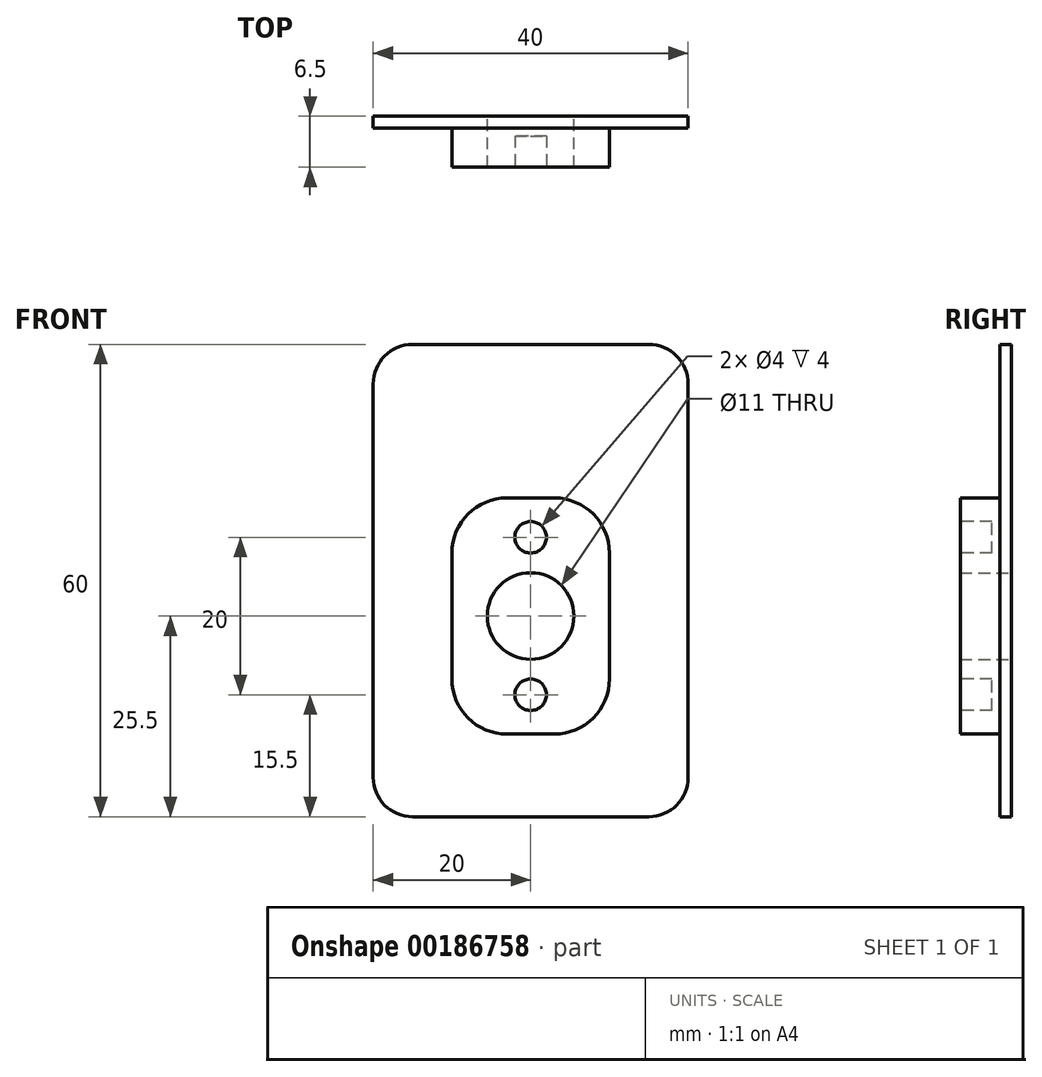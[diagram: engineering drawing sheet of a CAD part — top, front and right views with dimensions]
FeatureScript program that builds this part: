
annotation { "Feature Type Name" : "Feature", "Feature Type Description" : "" }
export const myFeature = defineFeature(function(context is Context, id is Id, definition is map)
    precondition{}
    {
        {
            var Q0;
            Q0=qCreatedBy(makeId("Front.planeOp"),FACE);
            var sketch = newSketch(context, id + "F0", { "sketchPlane" : qUnion([Q0])});
            skCircle(sketch, "E0", {"center": v(0, 0) * mm, "radius": 5.5 * mm});
            skLineSegment(sketch, "E1.bottom", {"start": v(20, -25.5) * mm, "end": v(-20, -25.5) * mm});
            skLineSegment(sketch, "E1.top", {"start": v(20, 34.5) * mm, "end": v(-20, 34.5) * mm});
            skLineSegment(sketch, "E1.left", {"start": v(20, -25.5) * mm, "end": v(20, 34.5) * mm});
            skLineSegment(sketch, "E1.right", {"start": v(-20, -25.5) * mm, "end": v(-20, 34.5) * mm});
            skSolve(sketch);
        }
        {
            var Q0;
            Q0=makeQuery(id+"F0.imprint","IMPRINT",FACE,{"disambiguationData":[TD([[makeQuery(id+"F0.imprint","IMPRINT",EDGE,{"derivedFrom":sQuery(id+"F0.wireOp",EDGE,"E0")}),-1.0]])]});
            extrude(context, id + "F1", {"entities" : qUnion([Q0]), "depth" : 1.5 * mm});
        }
        {
            var Q0;
            Q0=makeQuery(id+"F1.opExtrude","CAP_FACE",FACE,{"disambiguationData":[OSD([sQuery(id+"F0.wireOp",EDGE,"E0"),sQuery(id+"F0.wireOp",EDGE,"E1.bottom"),sQuery(id+"F0.wireOp",EDGE,"E1.top"),sQuery(id+"F0.wireOp",EDGE,"E1.left"),sQuery(id+"F0.wireOp",EDGE,"E1.right")])],"isStart":false});
            var sketch = newSketch(context, id + "F2", { "sketchPlane" : qUnion([Q0])});
            skLineSegment(sketch, "E2.bottom", {"start": v(-10, 15) * mm, "end": v(10, 15) * mm});
            skLineSegment(sketch, "E2.top", {"start": v(-10, -15) * mm, "end": v(10, -15) * mm});
            skLineSegment(sketch, "E2.left", {"start": v(-10, 15) * mm, "end": v(-10, -15) * mm});
            skLineSegment(sketch, "E2.right", {"start": v(10, 15) * mm, "end": v(10, -15) * mm});
            skPoint(sketch, "E2.middle", {"position": v(0, 0) * mm});
            skCircle(sketch, "E3", {"center": v(0, 0) * mm, "radius": 5.5 * mm});
            skSolve(sketch);
        }
        {
            var Q0;
            Q0 = qSketchRegion(id + "F2", true);
            extrude(context, id + "F3", {"entities" : qUnion([Q0]), "operationType" : NewBodyOperationType.ADD, "depth" : 5 * mm});
        }
        {
            var Q0;
            Q0=makeQuery(id+"F3.opExtrude","CAP_FACE",FACE,{"disambiguationData":[OSD([sQuery(id+"F2.wireOp",EDGE,"E2.bottom"),sQuery(id+"F2.wireOp",EDGE,"E2.top"),sQuery(id+"F2.wireOp",EDGE,"E2.left"),sQuery(id+"F2.wireOp",EDGE,"E2.right"),sQuery(id+"F2.wireOp",EDGE,"E3")])],"isStart":false});
            var sketch = newSketch(context, id + "F4", { "sketchPlane" : qUnion([Q0])});
            skCircle(sketch, "E4", {"center": v(0, 10) * mm, "radius": 2 * mm});
            skCircle(sketch, "E5", {"center": v(0, -10) * mm, "radius": 2 * mm});
            skSolve(sketch);
        }
        {
            var Q0;
            Q0 = qSketchRegion(id + "F4", true);
            extrude(context, id + "F5", {"entities" : qUnion([Q0]), "operationType" : NewBodyOperationType.REMOVE, "oppositeDirection" : true, "depth" : 4 * mm});
        }
        {
            var Q0;
            Q0=makeQuery(id+"F3.opExtrude","SWEPT_EDGE",EDGE,{"disambiguationData":[OSD([sQuery(id+"F2.wireOp",EDGE,"E2.bottom"),sQuery(id+"F2.wireOp",EDGE,"E2.right")])]});
            var Q1;
            Q1=makeQuery(id+"F3.opExtrude","SWEPT_EDGE",EDGE,{"disambiguationData":[OSD([sQuery(id+"F2.wireOp",EDGE,"E2.bottom"),sQuery(id+"F2.wireOp",EDGE,"E2.left")])]});
            var Q2;
            Q2=makeQuery(id+"F3.opExtrude","SWEPT_EDGE",EDGE,{"disambiguationData":[OSD([sQuery(id+"F2.wireOp",EDGE,"E2.top"),sQuery(id+"F2.wireOp",EDGE,"E2.right")])]});
            var Q3;
            Q3=makeQuery(id+"F3.opExtrude","SWEPT_EDGE",EDGE,{"disambiguationData":[OSD([sQuery(id+"F2.wireOp",EDGE,"E2.top"),sQuery(id+"F2.wireOp",EDGE,"E2.left")])]});
            fillet(context, id + "F6", {"entities" : qUnion([Q0, Q1, Q2, Q3]), "radius" : 7 * mm, "tangentPropagation" : true, "allowEdgeOverflow" : false});
        }
        {
            var Q0;
            Q0=makeQuery(id+"F1.opExtrude","SWEPT_EDGE",EDGE,{"disambiguationData":[OSD([sQuery(id+"F0.wireOp",EDGE,"E1.top"),sQuery(id+"F0.wireOp",EDGE,"E1.left")])]});
            var Q1;
            Q1=makeQuery(id+"F1.opExtrude","SWEPT_EDGE",EDGE,{"disambiguationData":[OSD([sQuery(id+"F0.wireOp",EDGE,"E1.bottom"),sQuery(id+"F0.wireOp",EDGE,"E1.left")])]});
            var Q2;
            Q2=makeQuery(id+"F1.opExtrude","SWEPT_EDGE",EDGE,{"disambiguationData":[OSD([sQuery(id+"F0.wireOp",EDGE,"E1.bottom"),sQuery(id+"F0.wireOp",EDGE,"E1.right")])]});
            var Q3;
            Q3=makeQuery(id+"F1.opExtrude","SWEPT_EDGE",EDGE,{"disambiguationData":[OSD([sQuery(id+"F0.wireOp",EDGE,"E1.top"),sQuery(id+"F0.wireOp",EDGE,"E1.right")])]});
            fillet(context, id + "F7", {"entities" : qUnion([Q0, Q1, Q2, Q3]), "radius" : 5 * mm, "tangentPropagation" : true, "allowEdgeOverflow" : false});
        }
    });
